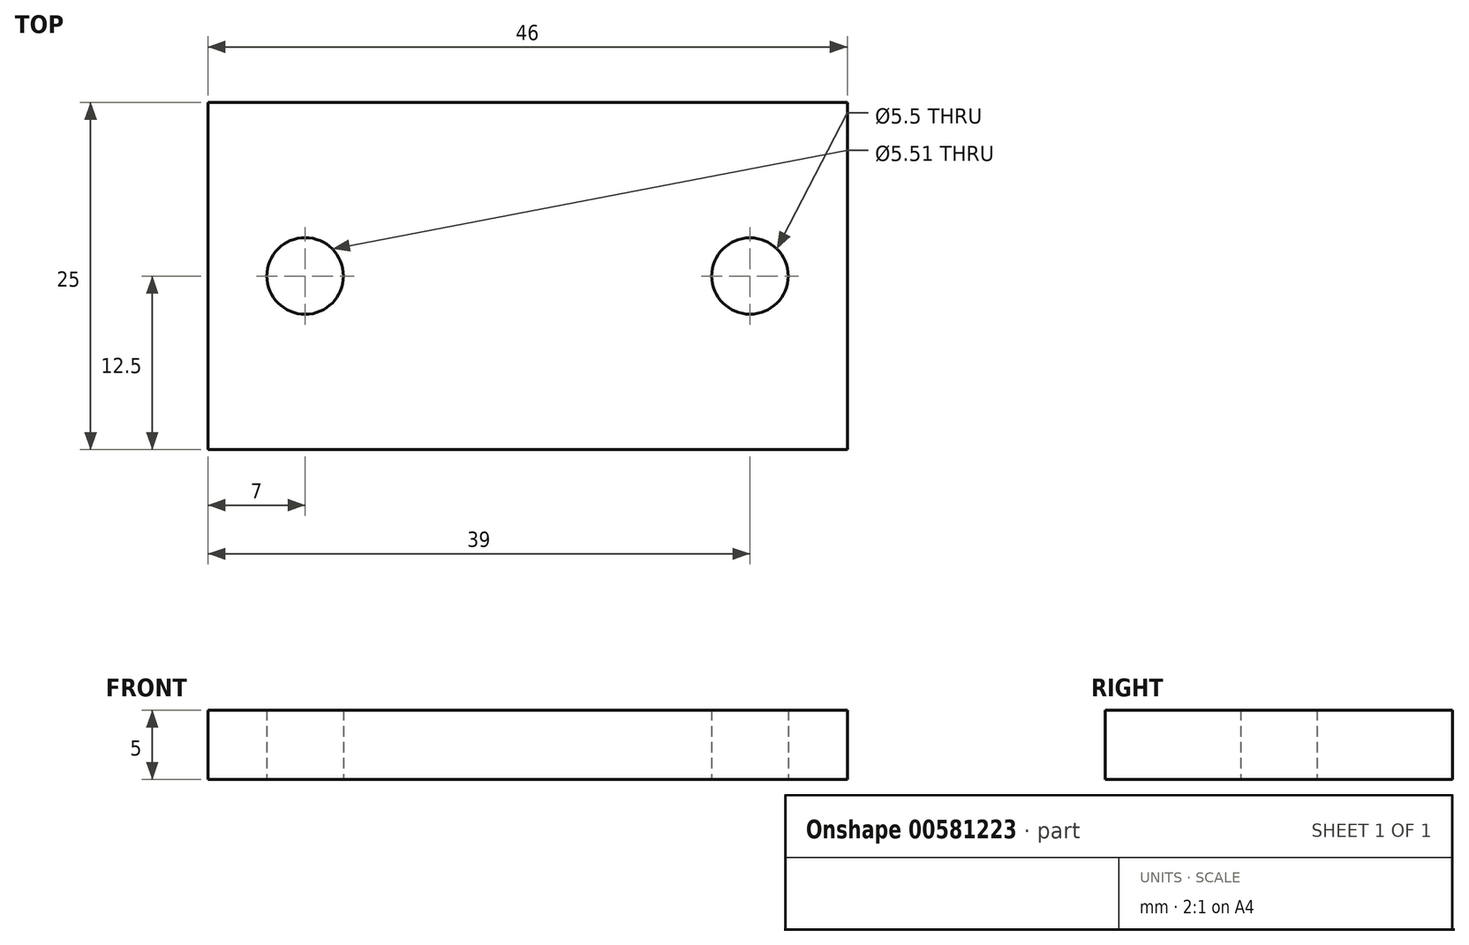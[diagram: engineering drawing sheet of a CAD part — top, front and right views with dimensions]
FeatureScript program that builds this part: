
annotation { "Feature Type Name" : "Feature", "Feature Type Description" : "" }
export const myFeature = defineFeature(function(context is Context, id is Id, definition is map)
    precondition{}
    {
        {
            var Q0;
            Q0=qCreatedBy(makeId("Top.planeOp"),FACE);
            var sketch = newSketch(context, id + "F0", { "sketchPlane" : qUnion([Q0])});
            skLineSegment(sketch, "E0.bottom", {"start": v(23, 12.5) * mm, "end": v(-23, 12.5) * mm});
            skLineSegment(sketch, "E0.top", {"start": v(23, -12.5) * mm, "end": v(-23, -12.5) * mm});
            skLineSegment(sketch, "E0.left", {"start": v(23, 12.5) * mm, "end": v(23, -12.5) * mm});
            skLineSegment(sketch, "E0.right", {"start": v(-23, 12.5) * mm, "end": v(-23, -12.5) * mm});
            skPoint(sketch, "E0.middle", {"position": v(0, 0) * mm});
            skCircle(sketch, "E1", {"center": v(16, 0) * mm, "radius": 2.75 * mm});
            skCircle(sketch, "E2.MirrorC", {"center": v(-16, 0) * mm, "radius": 2.76 * mm});
            skSolve(sketch);
        }
        {
            var Q0;
            Q0=qSketchRegion(id+"F0",true);
            extrude(context, id + "F1", {"entities" : qUnion([Q0]), "depth" : 5 * mm, "offsetDistance" : 25.4 * mm});
        }
    });
